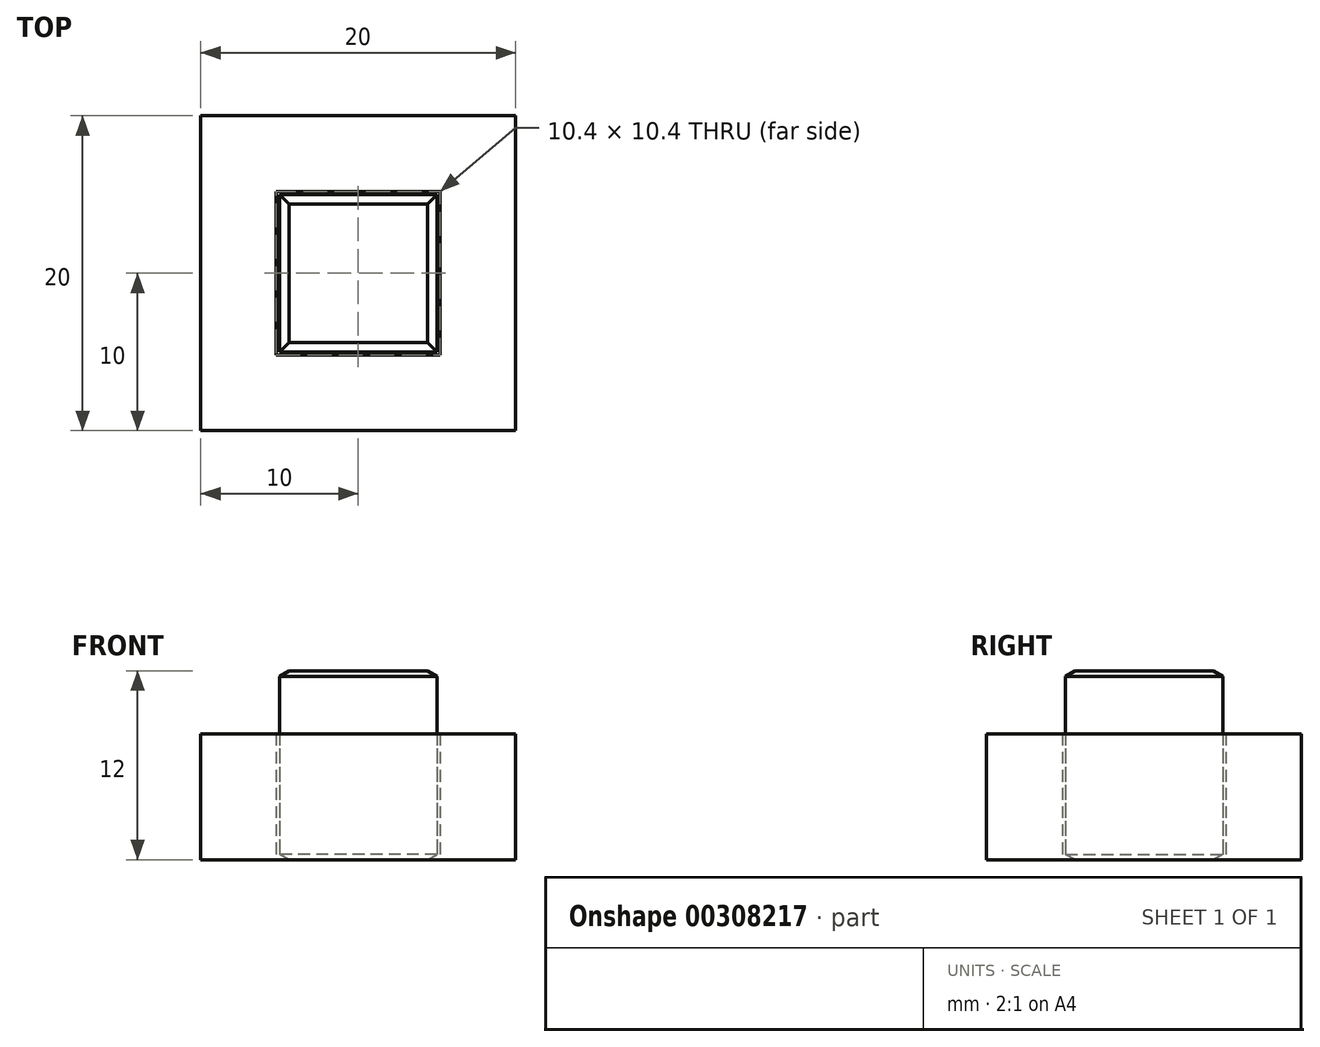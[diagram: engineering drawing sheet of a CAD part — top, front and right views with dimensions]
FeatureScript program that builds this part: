
annotation { "Feature Type Name" : "Feature", "Feature Type Description" : "" }
export const myFeature = defineFeature(function(context is Context, id is Id, definition is map)
    precondition{}
    {
        {
            var Q0;
            Q0=qCreatedBy(makeId("Top.planeOp"),FACE);
            var sketch = newSketch(context, id + "F0", { "sketchPlane" : qUnion([Q0])});
            skLineSegment(sketch, "E0.bottom", {"start": v(10, 10) * mm, "end": v(-10, 10) * mm});
            skLineSegment(sketch, "E0.top", {"start": v(10, -10) * mm, "end": v(-10, -10) * mm});
            skLineSegment(sketch, "E0.left", {"start": v(10, 10) * mm, "end": v(10, -10) * mm});
            skLineSegment(sketch, "E0.right", {"start": v(-10, 10) * mm, "end": v(-10, -10) * mm});
            skPoint(sketch, "E0.middle", {"position": v(0, 0) * mm});
            skLineSegment(sketch, "E1.bottom", {"start": v(5.2, 5.2) * mm, "end": v(-5.2, 5.2) * mm});
            skLineSegment(sketch, "E1.top", {"start": v(5.2, -5.2) * mm, "end": v(-5.2, -5.2) * mm});
            skLineSegment(sketch, "E1.left", {"start": v(5.2, 5.2) * mm, "end": v(5.2, -5.2) * mm});
            skLineSegment(sketch, "E1.right", {"start": v(-5.2, 5.2) * mm, "end": v(-5.2, -5.2) * mm});
            skLineSegment(sketch, "E2.bottom", {"start": v(5, 5) * mm, "end": v(-5, 5) * mm});
            skLineSegment(sketch, "E2.top", {"start": v(5, -5) * mm, "end": v(-5, -5) * mm});
            skLineSegment(sketch, "E2.left", {"start": v(5, 5) * mm, "end": v(5, -5) * mm});
            skLineSegment(sketch, "E2.right", {"start": v(-5, 5) * mm, "end": v(-5, -5) * mm});
            skSolve(sketch);
        }
        {
            var Q0;
            Q0=makeQuery(id+"F0.imprint","IMPRINT",FACE,{"disambiguationData":[TD([[makeQuery(id+"F0.imprint","IMPRINT",EDGE,{"derivedFrom":sQuery(id+"F0.wireOp",EDGE,"E2.bottom")}),1.0]])]});
            extrude(context, id + "F1", {"entities" : qUnion([Q0]), "depth" : 12 * mm, "offsetDistance" : 25 * mm});
        }
        {
            var Q0;
            Q0=makeQuery(id+"F0.imprint","IMPRINT",FACE,{"disambiguationData":[TD([[makeQuery(id+"F0.imprint","IMPRINT",EDGE,{"derivedFrom":sQuery(id+"F0.wireOp",EDGE,"E0.bottom")}),1.0]])]});
            extrude(context, id + "F2", {"entities" : qUnion([Q0]), "depth" : 8 * mm, "offsetDistance" : 25 * mm});
        }
        {
            var Q0;
            Q0=makeQuery(id+"F1.opExtrude","CAP_EDGE",EDGE,{"disambiguationData":[OSD([sQuery(id+"F0.wireOp",EDGE,"E2.right")])],"isStart":false});
            var Q1;
            Q1=makeQuery(id+"F1.opExtrude","CAP_EDGE",EDGE,{"disambiguationData":[OSD([sQuery(id+"F0.wireOp",EDGE,"E2.top")])],"isStart":false});
            var Q2;
            Q2=makeQuery(id+"F1.opExtrude","CAP_EDGE",EDGE,{"disambiguationData":[OSD([sQuery(id+"F0.wireOp",EDGE,"E2.bottom")])],"isStart":false});
            var Q3;
            Q3=makeQuery(id+"F1.opExtrude","CAP_EDGE",EDGE,{"disambiguationData":[OSD([sQuery(id+"F0.wireOp",EDGE,"E2.left")])],"isStart":false});
            var Q4;
            Q4=makeQuery(id+"F1.opExtrude","CAP_EDGE",EDGE,{"disambiguationData":[OSD([sQuery(id+"F0.wireOp",EDGE,"E2.left")])],"isStart":true});
            var Q5;
            Q5=makeQuery(id+"F1.opExtrude","CAP_EDGE",EDGE,{"disambiguationData":[OSD([sQuery(id+"F0.wireOp",EDGE,"E2.bottom")])],"isStart":true});
            var Q6;
            Q6=makeQuery(id+"F1.opExtrude","CAP_EDGE",EDGE,{"disambiguationData":[OSD([sQuery(id+"F0.wireOp",EDGE,"E2.top")])],"isStart":true});
            var Q7;
            Q7=makeQuery(id+"F1.opExtrude","CAP_EDGE",EDGE,{"disambiguationData":[OSD([sQuery(id+"F0.wireOp",EDGE,"E2.right")])],"isStart":true});
            chamfer(context, id + "F3", {"entities" : qUnion([Q0, Q1, Q2, Q3, Q4, Q5, Q6, Q7]), "chamferType" : ChamferType.OFFSET_ANGLE, "width" : .6 * mm, "oppositeDirection" : false, "angle" : 30 * degree, "tangentPropagation" : true});
        }
    });
